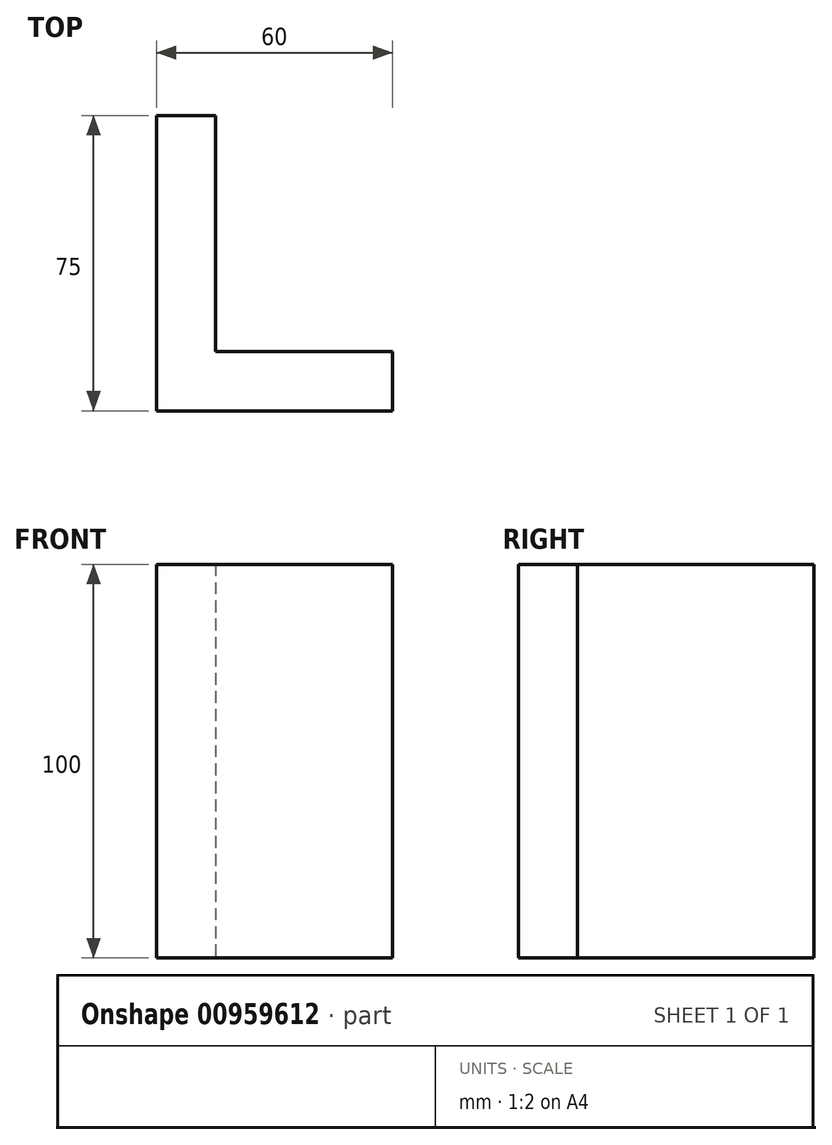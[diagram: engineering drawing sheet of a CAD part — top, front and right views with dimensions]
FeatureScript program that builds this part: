
annotation { "Feature Type Name" : "Feature", "Feature Type Description" : "" }
export const myFeature = defineFeature(function(context is Context, id is Id, definition is map)
    precondition{}
    {
        {
            var Q0;
            Q0=qCreatedBy(makeId("Top.planeOp"),FACE);
            var sketch = newSketch(context, id + "F0", { "sketchPlane" : qUnion([Q0])});
            skLineSegment(sketch, "E0", {"start": v(0, 75) * mm, "end": v(0, 0) * mm});
            skLineSegment(sketch, "E1", {"start": v(0, 0) * mm, "end": v(60, 0) * mm});
            skLineSegment(sketch, "E2", {"start": v(60, 0) * mm, "end": v(60, 15) * mm});
            skLineSegment(sketch, "E3", {"start": v(60, 15) * mm, "end": v(15, 15) * mm});
            skLineSegment(sketch, "E4", {"start": v(15, 15) * mm, "end": v(15, 75) * mm});
            skLineSegment(sketch, "E5", {"start": v(15, 75) * mm, "end": v(0, 75) * mm});
            skSolve(sketch);
        }
        {
            var Q0;
            Q0=makeQuery(id+"F0.imprint","IMPRINT",FACE,{"disambiguationData":[TD([[makeQuery(id+"F0.imprint","IMPRINT",EDGE,{"derivedFrom":sQuery(id+"F0.wireOp",EDGE,"E0")}),1.0]])]});
            extrude(context, id + "F1", {"entities" : qUnion([Q0]), "depth" : 100 * mm, "offsetDistance" : 25 * mm});
        }
    });
